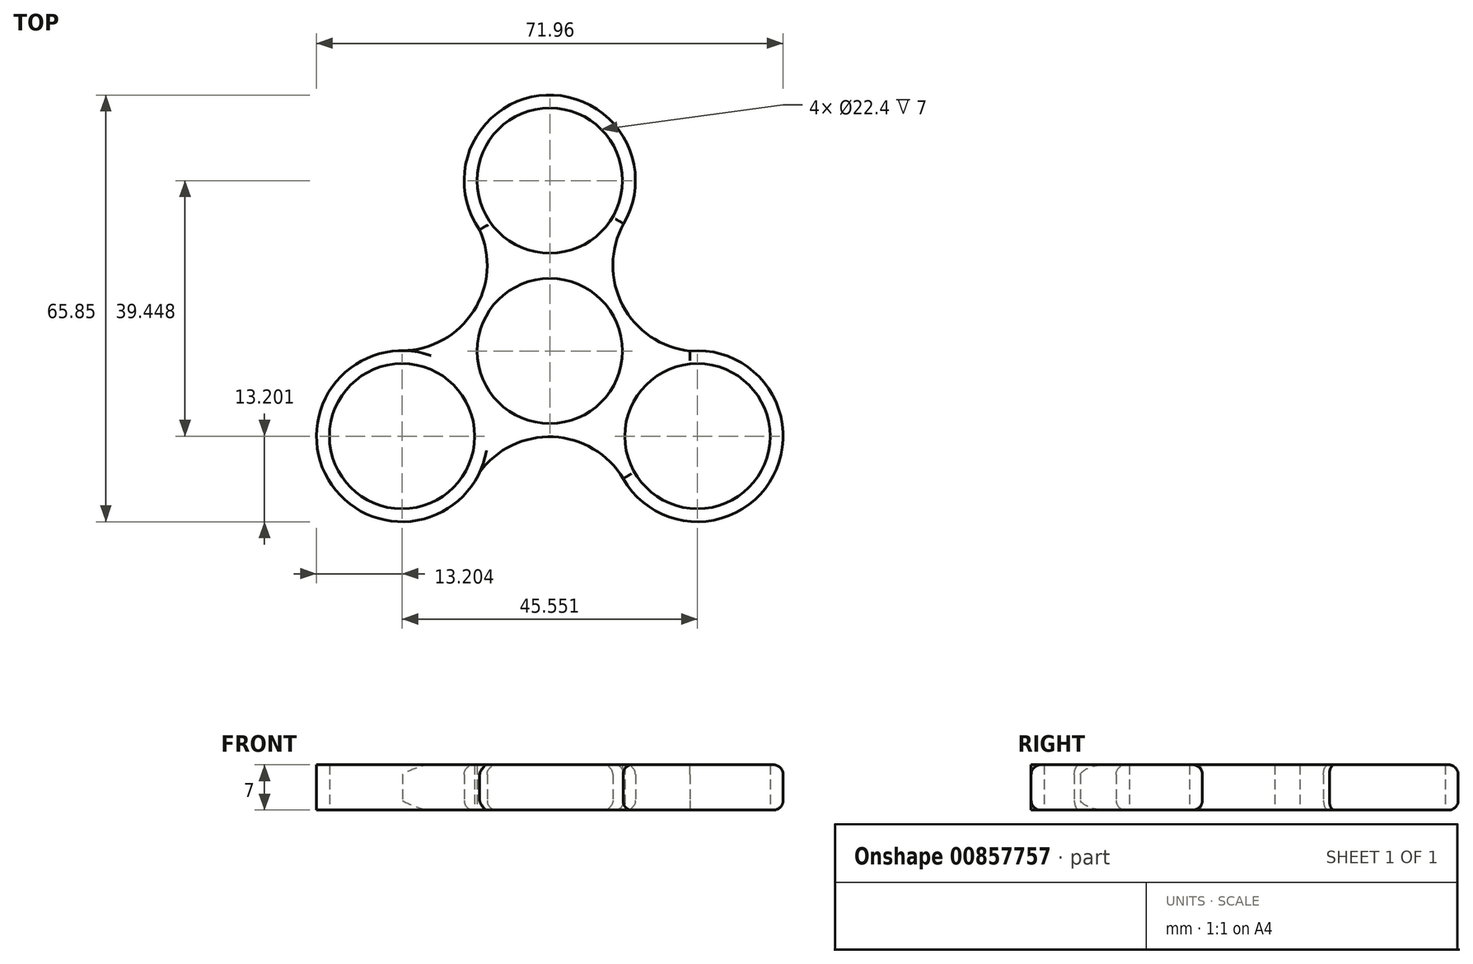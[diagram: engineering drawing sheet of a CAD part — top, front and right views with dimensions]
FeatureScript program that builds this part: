
annotation { "Feature Type Name" : "Feature", "Feature Type Description" : "" }
export const myFeature = defineFeature(function(context is Context, id is Id, definition is map)
    precondition{}
    {
        {
            var Q0;
            Q0=qCreatedBy(makeId("Top.planeOp"),FACE);
            var sketch = newSketch(context, id + "F0", { "sketchPlane" : qUnion([Q0])});
            skCircle(sketch, "E0", {"center": v(0, 0) * mm, "radius": 11.2 * mm});
            skCircle(sketch, "E1", {"center": v(0, 26.3) * mm, "radius": 11.2 * mm});
            skCircle(sketch, "E2.1.1", {"center": v(-22.78, -13.15) * mm, "radius": 11.2 * mm});
            skArc(sketch, "E2.2.0", {"start": v(11.31, -19.7) * mm, "mid": v(34.47, -19.27) * mm, "end": v(21.62, 0) * mm});
            skCircle(sketch, "E2.2.1", {"center": v(22.78, -13.15) * mm, "radius": 11.2 * mm});
            skArc(sketch, "E3.trimOffspring", {"start": v(-22.7, 0.05) * mm, "mid": v(-33.93, -20.21) * mm, "end": v(-10.81, -18.72) * mm});
            skArc(sketch, "E4.1.0", {"start": v(-22.7, 0.05) * mm, "mid": v(-11.73, 6.18) * mm, "end": v(-10.81, 18.72) * mm});
            skArc(sketch, "E4.2.0", {"start": v(11.31, -19.7) * mm, "mid": v(0.5, -13.25) * mm, "end": v(-10.81, -18.72) * mm});
            skArc(sketch, "E5.2.0", {"start": v(11.4, 19.64) * mm, "mid": v(11.22, 7.07) * mm, "end": v(21.62, 0) * mm});
            skArc(sketch, "E6.1.0", {"start": v(11.4, 19.64) * mm, "mid": v(-0.54, 39.49) * mm, "end": v(-10.81, 18.72) * mm});
            skSolve(sketch);
        }
        {
            var Q0;
            Q0=makeQuery(id+"F0.imprint","IMPRINT",FACE,{"disambiguationData":[TD([[makeQuery(id+"F0.imprint","IMPRINT",EDGE,{"derivedFrom":sQuery(id+"F0.wireOp",EDGE,"E0")}),-1.0]])]});
            extrude(context, id + "F1", {"entities" : qUnion([Q0]), "depth" : 7 * mm, "offsetDistance" : 25 * mm});
        }
        {
            var Q0;
            Q0=makeQuery(id+"F1.opExtrude","CAP_EDGE",EDGE,{"disambiguationData":[OSD([sQuery(id+"F0.wireOp",EDGE,"E4.2.0")])],"isStart":false});
            var Q1;
            Q1=makeQuery(id+"F1.opExtrude","CAP_EDGE",EDGE,{"disambiguationData":[OSD([sQuery(id+"F0.wireOp",EDGE,"E3.trimOffspring")])],"isStart":false});
            var Q2;
            Q2=makeQuery(id+"F1.opExtrude","CAP_EDGE",EDGE,{"disambiguationData":[OSD([sQuery(id+"F0.wireOp",EDGE,"E4.1.0")])],"isStart":false});
            var Q3;
            Q3=makeQuery(id+"F1.opExtrude","CAP_EDGE",EDGE,{"disambiguationData":[OSD([sQuery(id+"F0.wireOp",EDGE,"E6.1.0")])],"isStart":false});
            var Q4;
            Q4=makeQuery(id+"F1.opExtrude","CAP_EDGE",EDGE,{"disambiguationData":[OSD([sQuery(id+"F0.wireOp",EDGE,"E5.2.0")])],"isStart":false});
            var Q5;
            Q5=makeQuery(id+"F1.opExtrude","CAP_EDGE",EDGE,{"disambiguationData":[OSD([sQuery(id+"F0.wireOp",EDGE,"E2.2.0")])],"isStart":false});
            fillet(context, id + "F2", {"entities" : qUnion([Q0, Q1, Q2, Q3, Q4, Q5]), "radius" : 1.5 * mm, "tangentPropagation" : true, "allowEdgeOverflow" : false});
        }
        {
            var Q0;
            Q0=makeQuery(id+"F1.opExtrude","CAP_EDGE",EDGE,{"disambiguationData":[OSD([sQuery(id+"F0.wireOp",EDGE,"E4.2.0")])],"isStart":true});
            var Q1;
            Q1=makeQuery(id+"F1.opExtrude","CAP_EDGE",EDGE,{"disambiguationData":[OSD([sQuery(id+"F0.wireOp",EDGE,"E3.trimOffspring")])],"isStart":true});
            var Q2;
            Q2=makeQuery(id+"F1.opExtrude","CAP_EDGE",EDGE,{"disambiguationData":[OSD([sQuery(id+"F0.wireOp",EDGE,"E4.1.0")])],"isStart":true});
            var Q3;
            Q3=makeQuery(id+"F1.opExtrude","CAP_EDGE",EDGE,{"disambiguationData":[OSD([sQuery(id+"F0.wireOp",EDGE,"E6.1.0")])],"isStart":true});
            var Q4;
            Q4=makeQuery(id+"F1.opExtrude","CAP_EDGE",EDGE,{"disambiguationData":[OSD([sQuery(id+"F0.wireOp",EDGE,"E5.2.0")])],"isStart":true});
            var Q5;
            Q5=makeQuery(id+"F1.opExtrude","CAP_EDGE",EDGE,{"disambiguationData":[OSD([sQuery(id+"F0.wireOp",EDGE,"E2.2.0")])],"isStart":true});
            fillet(context, id + "F3", {"entities" : qUnion([Q0, Q1, Q2, Q3, Q4, Q5]), "radius" : 1.5 * mm, "tangentPropagation" : true, "allowEdgeOverflow" : false});
        }
    });
